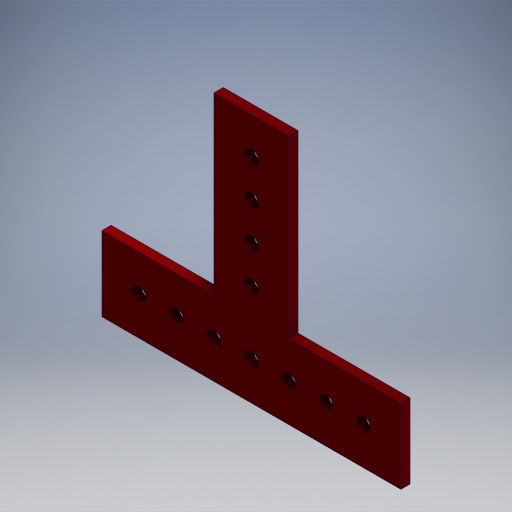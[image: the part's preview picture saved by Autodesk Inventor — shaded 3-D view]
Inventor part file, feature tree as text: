
AUTODESK INVENTOR PART (.ipt)
format: ipt  version: 2024.2 (Build 282272000, 272)  size: 290,304 bytes
history: native  units: in
note: dims shown in document units (in); Inventor stores cm internally (conversion verified against a paired STEP export)
features: extrude x1, sketch x1
ambient origin geometry x8: Origin, YZ Plane, XZ Plane, XY Plane, X Axis, Y Axis, Z Axis, Center Point
bodies: Solid1 (feature_tree)
feature tree (2):
  extrude  "Extrusion1"  Depth=0.125in
  sketch  "Sketch1"  dims[d0=0.196in d1=0.196in d2=0.846in d3=0.5in d4=0.25in d5=1.5748in d7=0.5in d8=0.3937in d10=1.0in d12=1.5748in d14=0.5in d15=0.3937in d17=1.0in d19=1.5748in d21=0.5in d22=0.3937in d24=1.0in d33=1.0in d34=0.125in d35=0.0in]
